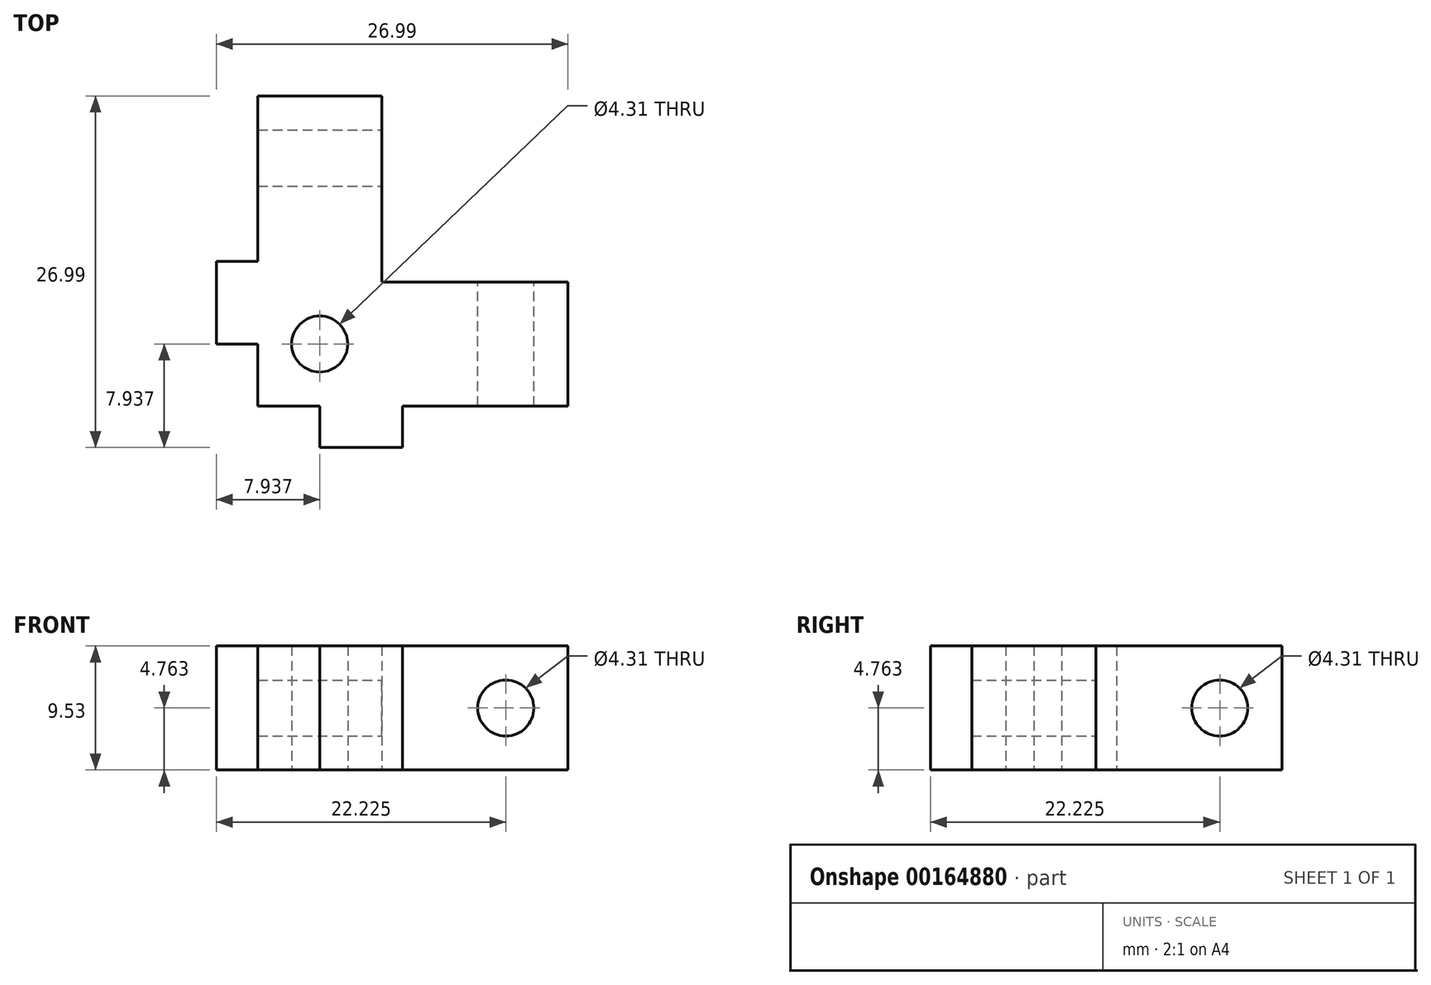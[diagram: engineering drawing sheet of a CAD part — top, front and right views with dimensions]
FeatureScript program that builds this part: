
annotation { "Feature Type Name" : "Feature", "Feature Type Description" : "" }
export const myFeature = defineFeature(function(context is Context, id is Id, definition is map)
    precondition{}
    {
        {
            var Q0;
            Q0=qCreatedBy(makeId("Top.planeOp"),FACE);
            var sketch = newSketch(context, id + "F0", { "sketchPlane" : qUnion([Q0])});
            skLineSegment(sketch, "E0.bottom", {"start": v(0, 0) * mm, "end": v(14.29, 0) * mm});
            skLineSegment(sketch, "E0.top", {"start": v(1.59, -9.52) * mm, "end": v(14.29, -9.52) * mm});
            skLineSegment(sketch, "E0.right", {"start": v(14.29, 0) * mm, "end": v(14.29, -9.53) * mm});
            skLineSegment(sketch, "E1.top", {"start": v(0, 14.29) * mm, "end": v(-9.53, 14.29) * mm});
            skLineSegment(sketch, "E1.left", {"start": v(0, 0) * mm, "end": v(0, 14.29) * mm});
            skLineSegment(sketch, "E1.right", {"start": v(-9.52, 1.59) * mm, "end": v(-9.53, 14.29) * mm});
            skLineSegment(sketch, "E2.bottom", {"start": v(1.59, -9.52) * mm, "end": v(-4.76, -9.52) * mm, "construction": true});
            skLineSegment(sketch, "E2.top", {"start": v(1.59, -12.7) * mm, "end": v(-4.76, -12.7) * mm});
            skLineSegment(sketch, "E2.left", {"start": v(1.59, -9.53) * mm, "end": v(1.59, -12.7) * mm});
            skLineSegment(sketch, "E2.right", {"start": v(-4.76, -9.53) * mm, "end": v(-4.76, -12.7) * mm});
            skLineSegment(sketch, "E3.bottom", {"start": v(-9.53, 1.59) * mm, "end": v(-12.7, 1.59) * mm});
            skLineSegment(sketch, "E3.top", {"start": v(-9.53, -4.76) * mm, "end": v(-12.7, -4.76) * mm});
            skLineSegment(sketch, "E3.left", {"start": v(-9.53, 1.59) * mm, "end": v(-9.52, -4.76) * mm, "construction": true});
            skLineSegment(sketch, "E3.right", {"start": v(-12.7, 1.59) * mm, "end": v(-12.7, -4.76) * mm});
            skLineSegment(sketch, "E4", {"start": v(-9.53, -4.76) * mm, "end": v(-9.53, -9.53) * mm});
            skLineSegment(sketch, "E5", {"start": v(-9.52, -9.53) * mm, "end": v(-4.76, -9.53) * mm});
            skLineSegment(sketch, "E6", {"start": v(14.29, 0) * mm, "end": v(14.29, 6.35) * mm, "construction": true});
            skLineSegment(sketch, "E7", {"start": v(14.29, 6.35) * mm, "end": v(6.35, 6.35) * mm, "construction": true});
            skLineSegment(sketch, "E8", {"start": v(0, 14.29) * mm, "end": v(6.35, 14.29) * mm, "construction": true});
            skLineSegment(sketch, "E9", {"start": v(6.35, 14.29) * mm, "end": v(6.35, 6.35) * mm, "construction": true});
            skLineSegment(sketch, "E10", {"start": v(-9.53, -4.76) * mm, "end": v(-4.76, -4.76) * mm, "construction": true});
            skLineSegment(sketch, "E11", {"start": v(-4.76, -4.76) * mm, "end": v(-4.76, -9.52) * mm, "construction": true});
            skCircle(sketch, "E12", {"center": v(-4.76, -4.76) * mm, "radius": 2.15 * mm});
            skSolve(sketch);
        }
        {
            var Q0;
            Q0 = qSketchRegion(id + "F0", true);
            extrude(context, id + "F1", {"entities" : qUnion([Q0]), "depth" : 9.52 * mm});
        }
        {
            var Q0;
            Q0=makeQuery(id+"F1.opExtrude","SWEPT_FACE",FACE,{"disambiguationData":[OSD([sQuery(id+"F0.wireOp",EDGE,"E0.bottom")])]});
            var sketch = newSketch(context, id + "F2", { "sketchPlane" : qUnion([Q0])});
            skLineSegment(sketch, "E13.bottom", {"start": v(-14.29, 4.76) * mm, "end": v(-9.53, 4.76) * mm, "construction": true});
            skLineSegment(sketch, "E13.top", {"start": v(-14.29, 0) * mm, "end": v(-9.53, 0) * mm, "construction": true});
            skLineSegment(sketch, "E13.left", {"start": v(-14.29, 4.76) * mm, "end": v(-14.29, 0) * mm, "construction": true});
            skLineSegment(sketch, "E13.right", {"start": v(-9.53, 4.76) * mm, "end": v(-9.53, 0) * mm, "construction": true});
            skCircle(sketch, "E14", {"center": v(-9.53, 4.76) * mm, "radius": 2.15 * mm});
            skSolve(sketch);
        }
        {
            var Q0;
            Q0 = qSketchRegion(id + "F2", true);
            var Q1;
            Q1=makeQuery(id+"F1.opExtrude","SWEPT_FACE",FACE,{"disambiguationData":[OSD([sQuery(id+"F0.wireOp",EDGE,"E0.top")])]});
            extrude(context, id + "F3", {"entities" : qUnion([Q0]), "operationType" : NewBodyOperationType.REMOVE, "endBound" : BoundingType.UP_TO_SURFACE, "oppositeDirection" : true, "endBoundEntityFace" : qUnion([Q1]), "depth" : 25.4 * mm});
        }
        {
            var Q0;
            Q0=makeQuery(id+"F1.opExtrude","SWEPT_FACE",FACE,{"disambiguationData":[OSD([sQuery(id+"F0.wireOp",EDGE,"E1.left")])]});
            var sketch = newSketch(context, id + "F4", { "sketchPlane" : qUnion([Q0])});
            skLineSegment(sketch, "E15.bottom", {"start": v(14.29, 4.76) * mm, "end": v(9.53, 4.76) * mm, "construction": true});
            skLineSegment(sketch, "E15.top", {"start": v(14.29, 0) * mm, "end": v(9.53, 0) * mm, "construction": true});
            skLineSegment(sketch, "E15.left", {"start": v(14.29, 4.76) * mm, "end": v(14.29, 0) * mm, "construction": true});
            skLineSegment(sketch, "E15.right", {"start": v(9.53, 4.76) * mm, "end": v(9.53, 0) * mm, "construction": true});
            skCircle(sketch, "E16", {"center": v(9.53, 4.76) * mm, "radius": 2.15 * mm});
            skSolve(sketch);
        }
        {
            var Q0;
            Q0 = qSketchRegion(id + "F4", true);
            var Q1;
            Q1=makeQuery(id+"F1.opExtrude","SWEPT_FACE",FACE,{"disambiguationData":[OSD([sQuery(id+"F0.wireOp",EDGE,"E1.right")])]});
            extrude(context, id + "F5", {"entities" : qUnion([Q0]), "operationType" : NewBodyOperationType.REMOVE, "endBound" : BoundingType.UP_TO_SURFACE, "oppositeDirection" : true, "endBoundEntityFace" : qUnion([Q1]), "depth" : 25.4 * mm});
        }
    });
